# Revit family: PURELIGHT-RP090-DAMCxxx
name_source: partatom
category: Leuchten
units: mm (PartAtom-declared; Revit-internal decimal feet)

## family parameters
Basisbauteil = Fläche
Beim Laden mit Abzugskörper schneiden = Nein
Bemaßung runder Anschluss = Durchmesser verwenden
Gemeinsam genutzt = Nein
Lichtquelle = Ja
OmniClass-Nummer = 23.80.70.11
OmniClass-Titel = Luminaries for Internal Lighting
Raumberechnungspunkt = Nein
Teiletyp = Normal

## types (3) — shared parameters
Baugruppenkennzeichen = D5020200
Datei für fotometrisches Netz = PURELIGHT-RP149 DAWS840O0650.IES
Emissionsform beim Rendern sichtbar = Nein
Farbfilter = 16777215
Farbtemperaturverschiebung bei Dämpfen der Lampe = <Keine Auswahl>
Hersteller = RIDI Leuchten GmbH
Lampe = LED
Neigungswinkel = 90.00°
Scheinlast = 26 VA
URL = www.spectral-lighting.com
Von Breite des Rechtecks ausssenden = 878 mm  [stored 2.88058 ft]
Von Länge des Rechtecks aussenden = 90 mm  [stored 0.295276 ft]
brand = Spectral
conformity mark = CE
electrical safety class = 1
height = 95 mm
ingress protection (IP) code = IP20
length = 903 mm  [stored 2.9626 ft]
nominal frequency = 50-60Hz
nominal voltage = 230
rated input power = 26
voltage type (AC, DC, UC) = AC
weight = 1,8 kg
width = 95 mm
zero-valued in all types: Vorgabe-Ansicht

## per-type parameters (varying)
| type | Modell |
| PURELIGHT-RP090 DAMC830O0350 | SPG0630381BB |
| PURELIGHT-RP090 DAMC840O0400 | SPG0630382BB |
| PURELIGHT-RP090 DAMC8TWO0350 | SPG0630383BB |

note: column(s) folded — value = type name in every type: product name

note: [stored X ft] marks values corroborated as IEEE doubles in the binary element streams (Revit-internal decimal feet)
